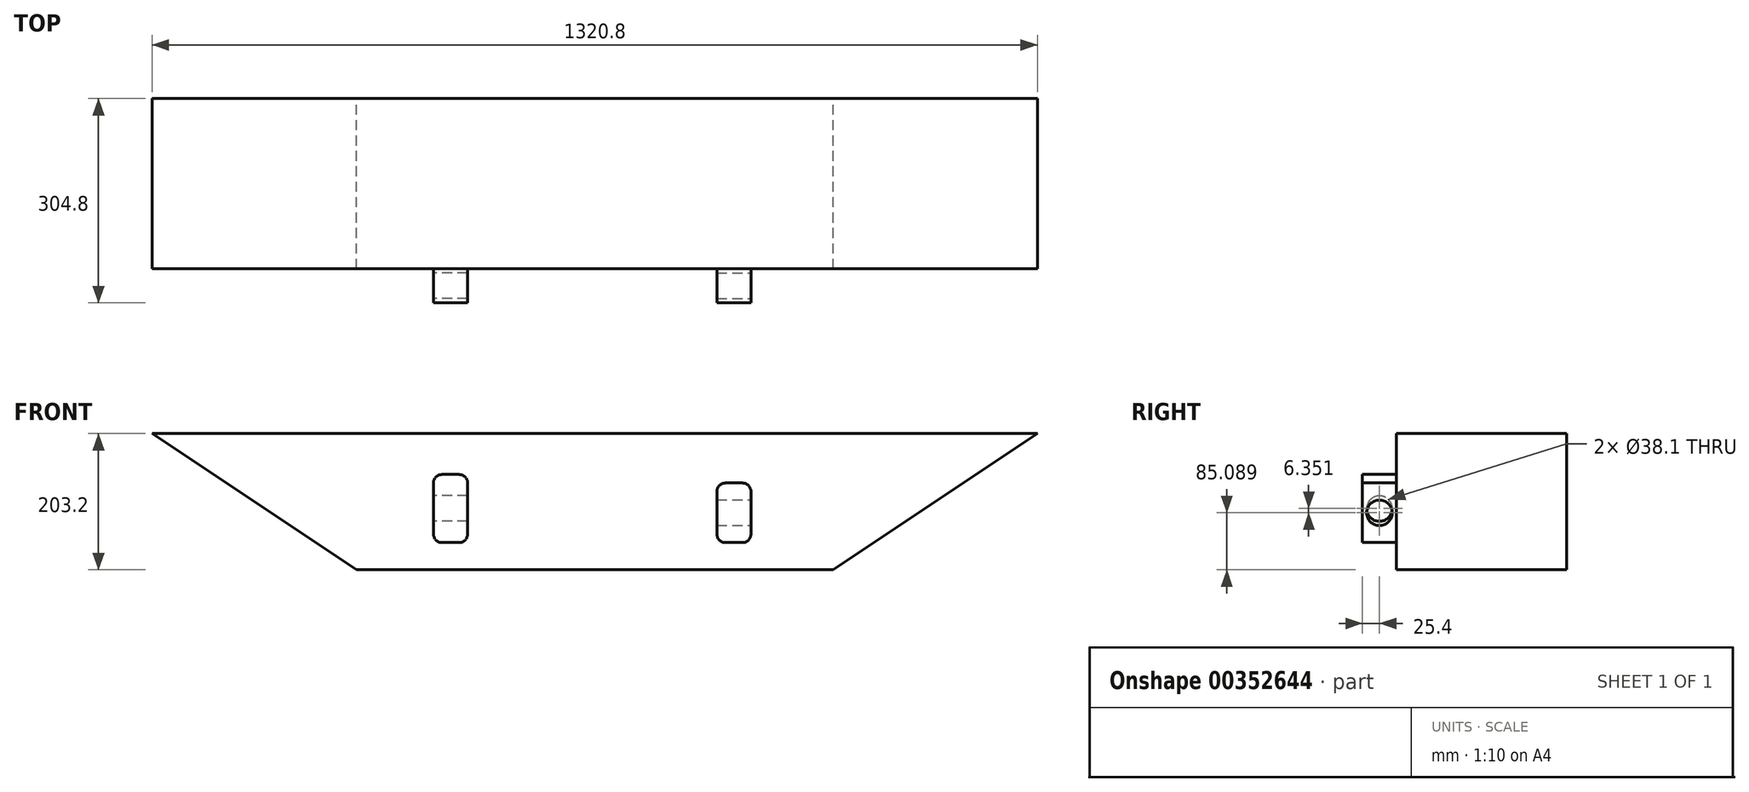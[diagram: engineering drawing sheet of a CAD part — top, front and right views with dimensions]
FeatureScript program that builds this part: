
annotation { "Feature Type Name" : "Feature", "Feature Type Description" : "" }
export const myFeature = defineFeature(function(context is Context, id is Id, definition is map)
    precondition{}
    {
        {
            var Q0;
            Q0=qCreatedBy(makeId("Front.planeOp"),FACE);
            var sketch = newSketch(context, id + "F0", { "sketchPlane" : qUnion([Q0])});
            skLineSegment(sketch, "E0.bottom", {"start": v(0, 0) * mm, "end": v(355.6, 0) * mm});
            skLineSegment(sketch, "E0.top", {"start": v(0, 203.2) * mm, "end": v(355.6, 203.2) * mm});
            skLineSegment(sketch, "E0.left", {"start": v(0, 0) * mm, "end": v(0, 203.2) * mm});
            skLineSegment(sketch, "E0.right", {"start": v(355.6, 0) * mm, "end": v(355.6, 203.2) * mm});
            skLineSegment(sketch, "E1.bottom", {"start": v(0, 0) * mm, "end": v(-355.6, 0) * mm});
            skLineSegment(sketch, "E1.top", {"start": v(0, 203.2) * mm, "end": v(-355.6, 203.2) * mm});
            skLineSegment(sketch, "E1.right", {"start": v(-355.6, 0) * mm, "end": v(-355.6, 203.2) * mm});
            skLineSegment(sketch, "E2", {"start": v(355.6, 0) * mm, "end": v(660.4, 203.2) * mm});
            skLineSegment(sketch, "E3", {"start": v(660.4, 203.2) * mm, "end": v(355.6, 203.2) * mm});
            skLineSegment(sketch, "E4", {"start": v(-355.6, 0) * mm, "end": v(-660.4, 203.2) * mm});
            skLineSegment(sketch, "E5", {"start": v(-660.4, 203.2) * mm, "end": v(-355.6, 203.2) * mm});
            skSolve(sketch);
        }
        {
            var Q0;
            Q0 = qSketchRegion(id + "F0", true);
            extrude(context, id + "F1", {"entities" : qUnion([Q0]), "depth" : 254 * mm});
        }
        {
            var Q0;
            Q0=makeQuery(id+"F1.opExtrude","CAP_FACE",FACE,{"disambiguationData":[OSD([sQuery(id+"F0.wireOp",EDGE,"E0.bottom"),sQuery(id+"F0.wireOp",EDGE,"E0.top"),sQuery(id+"F0.wireOp",EDGE,"E1.bottom"),sQuery(id+"F0.wireOp",EDGE,"E1.top"),sQuery(id+"F0.wireOp",EDGE,"E2"),sQuery(id+"F0.wireOp",EDGE,"E3"),sQuery(id+"F0.wireOp",EDGE,"E4"),sQuery(id+"F0.wireOp",EDGE,"E5")])],"isStart":false});
            var sketch = newSketch(context, id + "F2", { "sketchPlane" : qUnion([Q0])});
            skLineSegment(sketch, "E6.bottom", {"start": v(194.95, 129.54) * mm, "end": v(220.35, 129.54) * mm});
            skLineSegment(sketch, "E6.top", {"start": v(194.95, 40.64) * mm, "end": v(220.35, 40.64) * mm});
            skLineSegment(sketch, "E6.left", {"start": v(182.25, 116.84) * mm, "end": v(182.25, 53.34) * mm});
            skLineSegment(sketch, "E6.right", {"start": v(233.05, 116.84) * mm, "end": v(233.05, 53.34) * mm});
            skPoint(sketch, "E7.visualSharp", {"position": v(182.25, 40.64) * mm});
            skArc(sketch, "E7.filletArc", {"start": v(182.25, 53.34) * mm, "mid": v(185.97, 44.36) * mm, "end": v(194.95, 40.64) * mm});
            skPoint(sketch, "E8.visualSharp", {"position": v(233.05, 40.64) * mm});
            skArc(sketch, "E8.filletArc", {"start": v(220.35, 40.64) * mm, "mid": v(229.33, 44.36) * mm, "end": v(233.05, 53.34) * mm});
            skPoint(sketch, "E9.visualSharp", {"position": v(233.05, 129.54) * mm});
            skArc(sketch, "E9.filletArc", {"start": v(233.05, 116.84) * mm, "mid": v(229.33, 125.82) * mm, "end": v(220.35, 129.54) * mm});
            skPoint(sketch, "E10.visualSharp", {"position": v(182.25, 129.54) * mm});
            skArc(sketch, "E10.filletArc", {"start": v(194.95, 129.54) * mm, "mid": v(185.97, 125.82) * mm, "end": v(182.25, 116.84) * mm});
            skSolve(sketch);
        }
        {
            var Q0;
            Q0=makeQuery(id+"F2.imprint","IMPRINT",FACE,{"disambiguationData":[TD([[makeQuery(id+"F2.imprint","IMPRINT",EDGE,{"derivedFrom":sQuery(id+"F2.wireOp",EDGE,"E6.bottom")}),-1.0]])]});
            var sketch = newSketch(context, id + "F3", { "sketchPlane" : qUnion([Q0])});
            skSolve(sketch);
        }
        {
            var Q0;
            Q0=makeQuery(id+"F2.imprint","IMPRINT",FACE,{"disambiguationData":[TD([[makeQuery(id+"F2.imprint","IMPRINT",EDGE,{"derivedFrom":sQuery(id+"F2.wireOp",EDGE,"E6.bottom")}),1.0]])]});
            var sketch = newSketch(context, id + "F4", { "sketchPlane" : qUnion([Q0])});
            skLineSegment(sketch, "E11", {"start": v(356.65, 0) * mm, "end": v(356.65, 203.58) * mm});
            skLineSegment(sketch, "E12.bottom", {"start": v(-227.83, 40.64) * mm, "end": v(-202.43, 40.64) * mm});
            skLineSegment(sketch, "E12.top", {"start": v(-227.83, 142.24) * mm, "end": v(-202.43, 142.24) * mm});
            skLineSegment(sketch, "E12.left", {"start": v(-240.53, 53.34) * mm, "end": v(-240.53, 129.54) * mm});
            skLineSegment(sketch, "E12.right", {"start": v(-189.73, 53.34) * mm, "end": v(-189.73, 129.54) * mm});
            skLineSegment(sketch, "E13", {"start": v(-364.12, 0) * mm, "end": v(-364.12, 208.4) * mm});
            skLineSegment(sketch, "E14", {"start": v(160.32, 0) * mm, "end": v(259.43, 0) * mm});
            skLineSegment(sketch, "E15", {"start": v(259.43, 0) * mm, "end": v(160.32, 0) * mm});
            skLineSegment(sketch, "E16", {"start": v(-255.73, 0) * mm, "end": v(-154.17, 0) * mm});
            skPoint(sketch, "E17.visualSharp", {"position": v(-240.53, 40.64) * mm});
            skArc(sketch, "E17.filletArc", {"start": v(-240.53, 53.34) * mm, "mid": v(-236.8, 44.36) * mm, "end": v(-227.83, 40.64) * mm});
            skPoint(sketch, "E18.visualSharp", {"position": v(-189.73, 40.64) * mm});
            skArc(sketch, "E18.filletArc", {"start": v(-202.43, 40.64) * mm, "mid": v(-193.45, 44.36) * mm, "end": v(-189.73, 53.34) * mm});
            skPoint(sketch, "E19.visualSharp", {"position": v(-240.53, 142.24) * mm});
            skArc(sketch, "E19.filletArc", {"start": v(-227.83, 142.24) * mm, "mid": v(-236.8, 138.52) * mm, "end": v(-240.53, 129.54) * mm});
            skPoint(sketch, "E20.visualSharp", {"position": v(-189.73, 142.24) * mm});
            skArc(sketch, "E20.filletArc", {"start": v(-189.73, 129.54) * mm, "mid": v(-193.45, 138.52) * mm, "end": v(-202.43, 142.24) * mm});
            skSolve(sketch);
        }
        {
            var Q0;
            Q0 = qSketchRegion(id + "F4", true);
            var Q1;
            Q1=makeQuery(id+"F3.imprint","IMPRINT",FACE,{"disambiguationData":[TD([[makeQuery(id+"F3.imprint","IMPRINT",EDGE,{"derivedFrom":makeQuery(id+"F2.imprint","IMPRINT",EDGE,{"derivedFrom":sQuery(id+"F2.wireOp",EDGE,"E6.bottom")})}),-1.0]])]});
            extrude(context, id + "F5", {"entities" : qUnion([Q0, Q1]), "operationType" : NewBodyOperationType.ADD, "depth" : 50.8 * mm});
        }
        {
            var Q0;
            Q0=makeQuery(id+"F5.opExtrude","SWEPT_FACE",FACE,{"disambiguationData":[OSD([sQuery(id+"F2.wireOp",EDGE,"E6.right")])]});
            var sketch = newSketch(context, id + "F6", { "sketchPlane" : qUnion([Q0])});
            skCircle(sketch, "E21", {"center": v(-279.4, 85.09) * mm, "radius": 19.05 * mm});
            skSolve(sketch);
        }
        {
            var Q0;
            Q0 = qSketchRegion(id + "F6", true);
            extrude(context, id + "F7", {"entities" : qUnion([Q0]), "operationType" : NewBodyOperationType.REMOVE, "oppositeDirection" : true, "depth" : 50.8 * mm});
        }
        {
            var Q0;
            Q0=makeQuery(id+"F5.opExtrude","SWEPT_FACE",FACE,{"disambiguationData":[OSD([sQuery(id+"F4.wireOp",EDGE,"E12.left")])]});
            var sketch = newSketch(context, id + "F8", { "sketchPlane" : qUnion([Q0])});
            skCircle(sketch, "E22", {"center": v(279.4, 91.44) * mm, "radius": 19.05 * mm});
            skSolve(sketch);
        }
        {
            var Q0;
            Q0=makeQuery(id+"F8.imprint","IMPRINT",FACE,{"disambiguationData":[TD([[makeQuery(id+"F8.imprint","IMPRINT",EDGE,{"derivedFrom":sQuery(id+"F8.wireOp",EDGE,"E22")}),1.0]])]});
            extrude(context, id + "F9", {"entities" : qUnion([Q0]), "operationType" : NewBodyOperationType.REMOVE, "oppositeDirection" : true, "depth" : 50.8 * mm});
        }
    });
